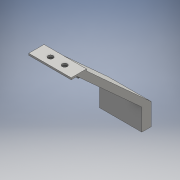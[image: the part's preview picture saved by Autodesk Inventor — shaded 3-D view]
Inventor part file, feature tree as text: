
AUTODESK INVENTOR PART (.ipt)
format: ipt  version: 2016 (Build 200138000, 138)  size: 159,744 bytes
history: native  units: mm
features: sketch x5, extrude x3, hole x2
ambient origin geometry x8: Origin, YZ Plane, XZ Plane, XY Plane, X Axis, Y Axis, Z Axis, Center Point
bodies: Solid1 (feature_tree)
feature tree (10):
  extrude  "Extrusion1"  Depth=1.5mm
  hole  "Hole1"  [1 undecoded]
  hole  "Hole2"  [1 undecoded]
  extrude  "Extrusion3"  Depth=1.5mm
  extrude  "Extrusion4"  Depth=12.0mm
  sketch  "Sketch1"  dims[d4=13.0mm d5=1.5mm]
  sketch  "Sketch3"  dims[d6=50.0mm d7=55.0mm]
  sketch  "Sketch5"  dims[d8=18.5mm d9=8.0mm]
  sketch  "Sketch6"  dims[d10=1.5mm d11=5.0mm]
  sketch  "Sketch7"  dims[d12=36.0mm d13=0.0mm d20=4.0mm d21=4.35mm d22=4.35mm d23=6.0mm d24=6.0mm d25=4.35mm d26=6.0mm d27=4.0mm d28=2.0mm d29=90.0deg d30=8.0mm d31=20.594885mm d35=13.0mm d36=4.35mm d37=6.0mm d38=4.35mm d39=6.0mm d40=4.35mm d41=6.0mm d42=4.0mm d43=2.0mm d44=90.0deg d45=8.0mm d46=20.594885mm d47=6.0mm d48=6.0mm d49=8.0mm d50=24.0mm d51=90.0deg d52=7.0mm d53=0.0mm d54=24.0mm d55=12.0mm d56=0.0mm]
note: 2 required parameter values undecoded (feature->parameter linkage not recoverable at this tier; creation-order binding heuristic only, values carry confidence <= 0.55)
